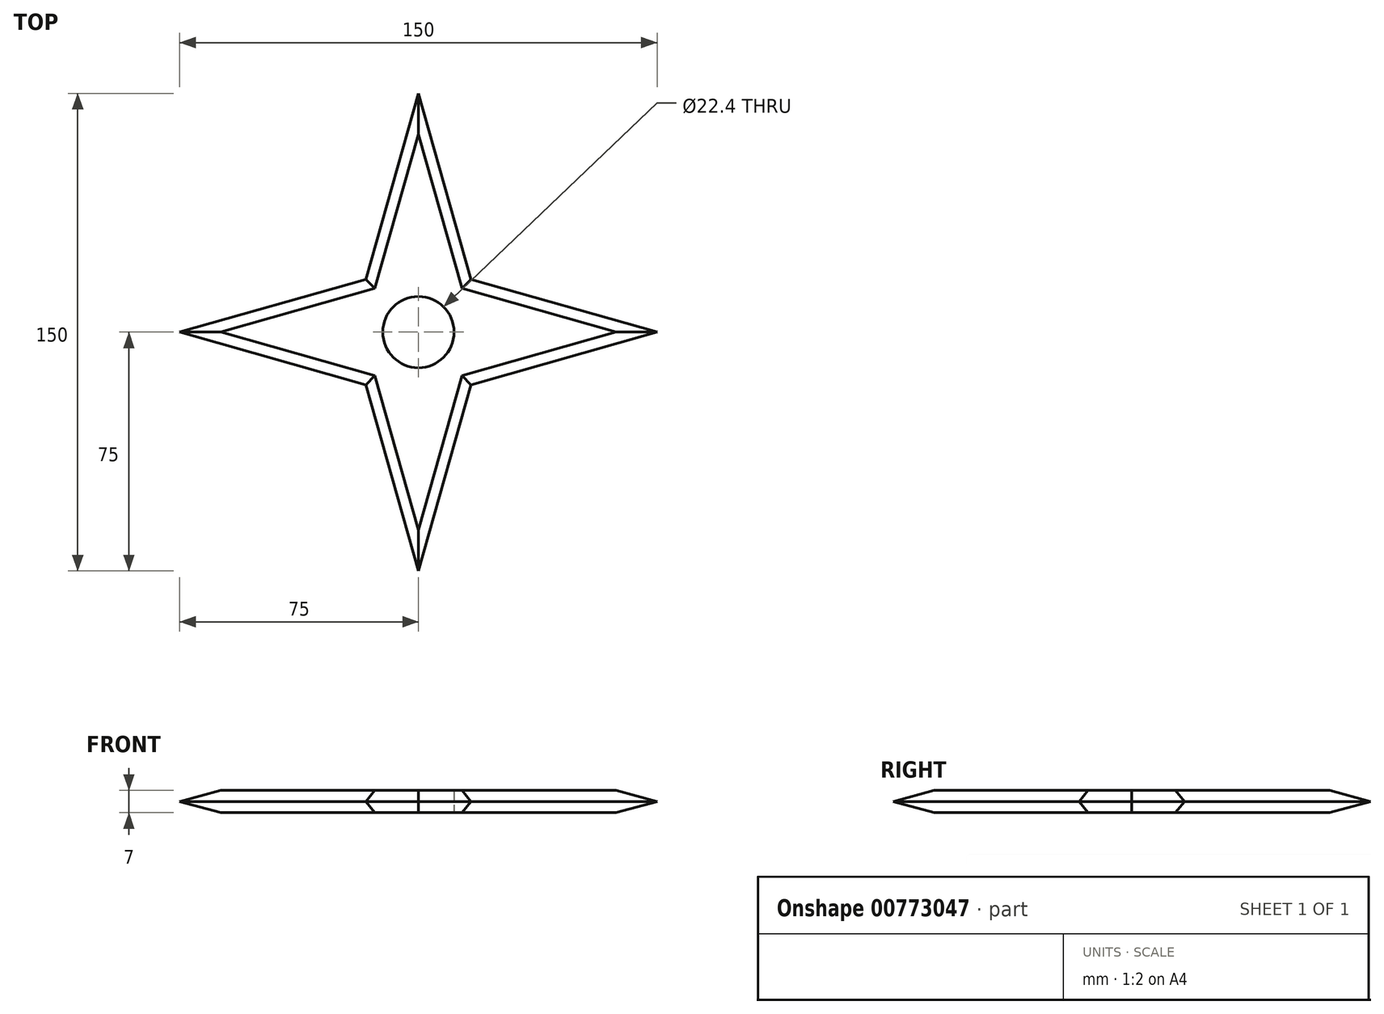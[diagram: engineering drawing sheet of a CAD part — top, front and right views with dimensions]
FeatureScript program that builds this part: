
annotation { "Feature Type Name" : "Feature", "Feature Type Description" : "" }
export const myFeature = defineFeature(function(context is Context, id is Id, definition is map)
    precondition{}
    {
        {
            var Q0;
            Q0=qCreatedBy(makeId("Top.planeOp"),FACE);
            var sketch = newSketch(context, id + "F0", { "sketchPlane" : qUnion([Q0])});
            skPoint(sketch, "E0.center", {"position": v(0, 0) * mm});
            skLineSegment(sketch, "E1", {"start": v(-75, 0) * mm, "end": v(75, 0) * mm});
            skLineSegment(sketch, "E2.1.0", {"start": v(0, 75) * mm, "end": v(0, -75) * mm});
            skLineSegment(sketch, "E2.anchor1", {"start": v(0, 0) * mm, "end": v(-75, 0) * mm, "construction": true});
            skLineSegment(sketch, "E2.anchor2", {"start": v(0, 0) * mm, "end": v(0, 75) * mm, "construction": true});
            skCircle(sketch, "E3", {"center": v(0, 0) * mm, "radius": 11.2 * mm});
            skLineSegment(sketch, "E4", {"start": v(0, 75) * mm, "end": v(-16.54, 16.54) * mm});
            skLineSegment(sketch, "E5", {"start": v(-16.54, 16.54) * mm, "end": v(-75, 0) * mm});
            skLineSegment(sketch, "E6", {"start": v(-75, 0) * mm, "end": v(-16.54, -16.54) * mm});
            skLineSegment(sketch, "E7", {"start": v(-16.54, -16.54) * mm, "end": v(0, -75) * mm});
            skLineSegment(sketch, "E8", {"start": v(0, -75) * mm, "end": v(16.54, -16.54) * mm});
            skLineSegment(sketch, "E9", {"start": v(16.54, -16.54) * mm, "end": v(75, 0) * mm});
            skLineSegment(sketch, "E10", {"start": v(75, 0) * mm, "end": v(16.54, 16.54) * mm});
            skLineSegment(sketch, "E11", {"start": v(16.54, 16.54) * mm, "end": v(0, 75) * mm});
            skPoint(sketch, "E12.orphan", {"position": v(-76.2, 76.2) * mm});
            skPoint(sketch, "E13.orphan", {"position": v(76.2, 76.2) * mm});
            skLineSegment(sketch, "E14.trimOffspring", {"start": v(-76.2, -76.2) * mm, "end": v(-76.2, -76.2) * mm, "construction": true});
            skLineSegment(sketch, "E15.trimOffspring", {"start": v(-76.2, -76.2) * mm, "end": v(-76.2, -76.2) * mm});
            skPoint(sketch, "E16.orphan", {"position": v(76.2, -76.2) * mm});
            skSolve(sketch);
        }
        {
            var Q0;
            {var subQ0=sQuery(id+"F0.wireOp",EDGE,"E4");Q0=makeQuery(id+"F0.imprint","IMPRINT",FACE,{"disambiguationData":[TD([[makeQuery(id+"F0.imprint","IMPRINT",EDGE,{"derivedFrom":subQ0}),1.0]])]});}
            var Q1;
            {var subQ4=sQuery(id+"F0.wireOp",EDGE,"E10");Q1=makeQuery(id+"F0.imprint","IMPRINT",FACE,{"disambiguationData":[TD([[makeQuery(id+"F0.imprint","IMPRINT",EDGE,{"derivedFrom":subQ4}),1.0]])]});}
            var Q2;
            {var subQ0=sQuery(id+"F0.wireOp",EDGE,"E8");Q2=makeQuery(id+"F0.imprint","IMPRINT",FACE,{"disambiguationData":[TD([[makeQuery(id+"F0.imprint","IMPRINT",EDGE,{"derivedFrom":subQ0}),1.0]])]});}
            var Q3;
            {var subQ0=sQuery(id+"F0.wireOp",EDGE,"E6");Q3=makeQuery(id+"F0.imprint","IMPRINT",FACE,{"disambiguationData":[TD([[makeQuery(id+"F0.imprint","IMPRINT",EDGE,{"derivedFrom":subQ0}),1.0]])]});}
            extrude(context, id + "F1", {"entities" : qUnion([Q0, Q1, Q2, Q3]), "depth" : 7 * mm, "offsetDistance" : 25 * mm});
        }
        {
            var Q0;
            Q0=makeQuery(id+"F1.opExtrude","CAP_EDGE",EDGE,{"disambiguationData":[OSD([sQuery(id+"F0.wireOp",EDGE,"E6")])],"isStart":false});
            var Q1;
            Q1=makeQuery(id+"F1.opExtrude","CAP_EDGE",EDGE,{"disambiguationData":[OSD([sQuery(id+"F0.wireOp",EDGE,"E7")])],"isStart":false});
            var Q2;
            Q2=makeQuery(id+"F1.opExtrude","CAP_EDGE",EDGE,{"disambiguationData":[OSD([sQuery(id+"F0.wireOp",EDGE,"E8")])],"isStart":false});
            var Q3;
            Q3=makeQuery(id+"F1.opExtrude","CAP_EDGE",EDGE,{"disambiguationData":[OSD([sQuery(id+"F0.wireOp",EDGE,"E9")])],"isStart":false});
            var Q4;
            Q4=makeQuery(id+"F1.opExtrude","CAP_EDGE",EDGE,{"disambiguationData":[OSD([sQuery(id+"F0.wireOp",EDGE,"E10")])],"isStart":false});
            var Q5;
            Q5=makeQuery(id+"F1.opExtrude","CAP_EDGE",EDGE,{"disambiguationData":[OSD([sQuery(id+"F0.wireOp",EDGE,"E11")])],"isStart":false});
            var Q6;
            Q6=makeQuery(id+"F1.opExtrude","CAP_EDGE",EDGE,{"disambiguationData":[OSD([sQuery(id+"F0.wireOp",EDGE,"E4")])],"isStart":false});
            var Q7;
            Q7=makeQuery(id+"F1.opExtrude","CAP_EDGE",EDGE,{"disambiguationData":[OSD([sQuery(id+"F0.wireOp",EDGE,"E5")])],"isStart":false});
            chamfer(context, id + "F2", {"entities" : qUnion([Q0, Q1, Q2, Q3, Q4, Q5, Q6, Q7]), "width" : 3.5 * mm, "tangentPropagation" : true});
        }
        {
            var Q0;
            Q0=makeQuery(id+"F1.opExtrude","CAP_EDGE",EDGE,{"disambiguationData":[OSD([sQuery(id+"F0.wireOp",EDGE,"E6")])],"isStart":true});
            var Q1;
            Q1=makeQuery(id+"F1.opExtrude","CAP_EDGE",EDGE,{"disambiguationData":[OSD([sQuery(id+"F0.wireOp",EDGE,"E5")])],"isStart":true});
            var Q2;
            Q2=makeQuery(id+"F1.opExtrude","CAP_EDGE",EDGE,{"disambiguationData":[OSD([sQuery(id+"F0.wireOp",EDGE,"E4")])],"isStart":true});
            var Q3;
            Q3=makeQuery(id+"F1.opExtrude","CAP_EDGE",EDGE,{"disambiguationData":[OSD([sQuery(id+"F0.wireOp",EDGE,"E11")])],"isStart":true});
            var Q4;
            Q4=makeQuery(id+"F1.opExtrude","CAP_EDGE",EDGE,{"disambiguationData":[OSD([sQuery(id+"F0.wireOp",EDGE,"E10")])],"isStart":true});
            var Q5;
            Q5=makeQuery(id+"F1.opExtrude","CAP_EDGE",EDGE,{"disambiguationData":[OSD([sQuery(id+"F0.wireOp",EDGE,"E9")])],"isStart":true});
            var Q6;
            Q6=makeQuery(id+"F1.opExtrude","CAP_EDGE",EDGE,{"disambiguationData":[OSD([sQuery(id+"F0.wireOp",EDGE,"E8")])],"isStart":true});
            var Q7;
            Q7=makeQuery(id+"F1.opExtrude","CAP_EDGE",EDGE,{"disambiguationData":[OSD([sQuery(id+"F0.wireOp",EDGE,"E7")])],"isStart":true});
            chamfer(context, id + "F3", {"entities" : qUnion([Q0, Q1, Q2, Q3, Q4, Q5, Q6, Q7]), "width" : 3.5 * mm, "tangentPropagation" : true});
        }
    });
